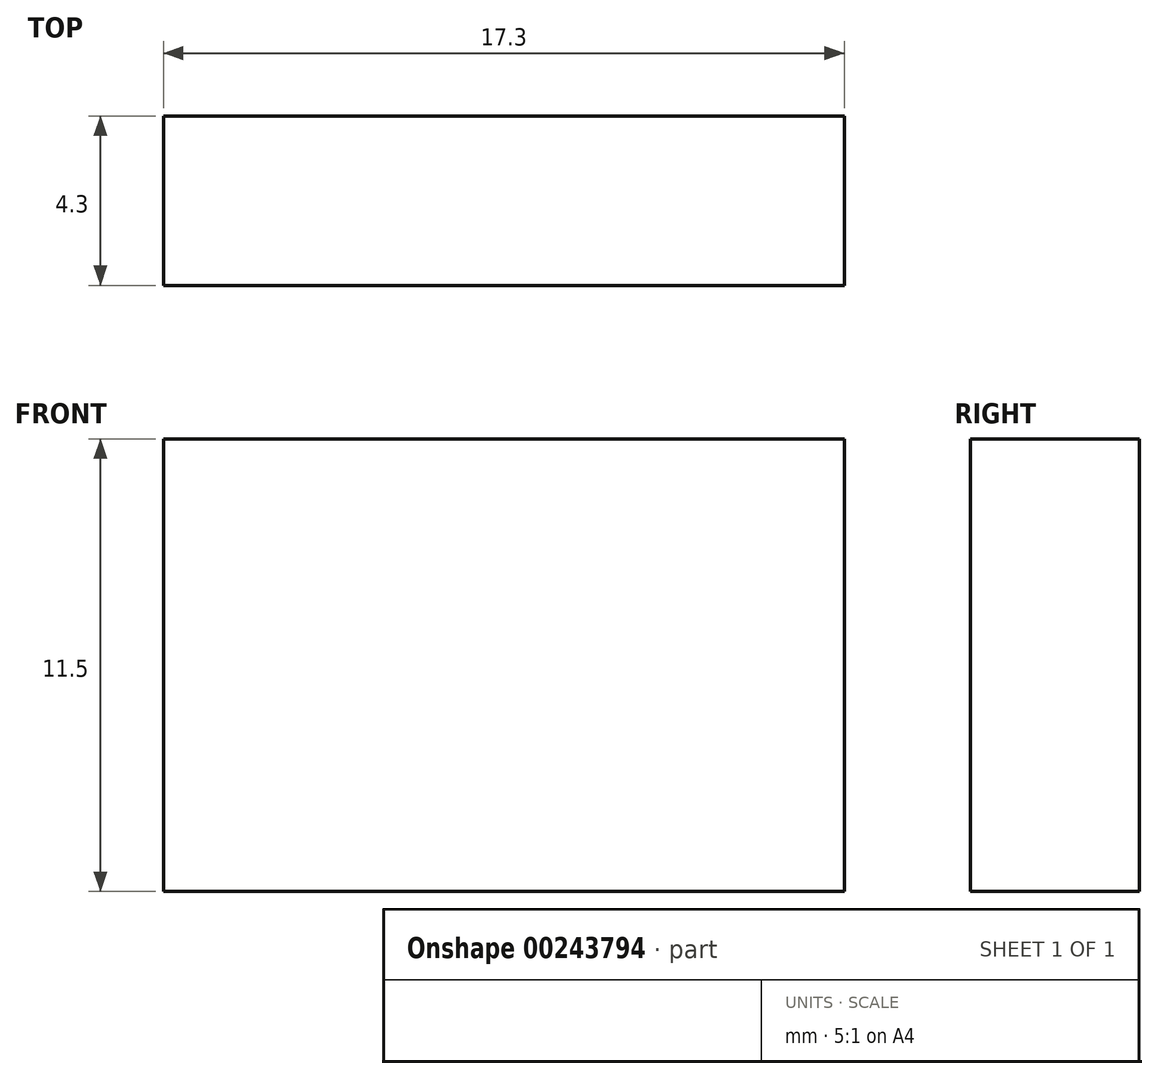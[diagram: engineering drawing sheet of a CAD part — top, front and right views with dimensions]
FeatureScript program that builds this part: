
annotation { "Feature Type Name" : "Feature", "Feature Type Description" : "" }
export const myFeature = defineFeature(function(context is Context, id is Id, definition is map)
    precondition{}
    {
        {
            var Q0;
            Q0=qCreatedBy(makeId("Front.planeOp"),FACE);
            var sketch = newSketch(context, id + "F0", { "sketchPlane" : qUnion([Q0])});
            skLineSegment(sketch, "E0.bottom", {"start": v(8.65, -5.75) * mm, "end": v(-8.65, -5.75) * mm});
            skLineSegment(sketch, "E0.top", {"start": v(8.65, 5.75) * mm, "end": v(-8.65, 5.75) * mm});
            skLineSegment(sketch, "E0.left", {"start": v(8.65, -5.75) * mm, "end": v(8.65, 5.75) * mm});
            skLineSegment(sketch, "E0.right", {"start": v(-8.65, -5.75) * mm, "end": v(-8.65, 5.75) * mm});
            skPoint(sketch, "E0.middle", {"position": v(0, 0) * mm});
            skSolve(sketch);
        }
        {
            var Q0;
            Q0 = qSketchRegion(id + "F0", true);
            extrude(context, id + "F1", {"entities" : qUnion([Q0]), "endBound" : BoundingType.SYMMETRIC, "depth" : 4.3 * mm});
        }
    });
